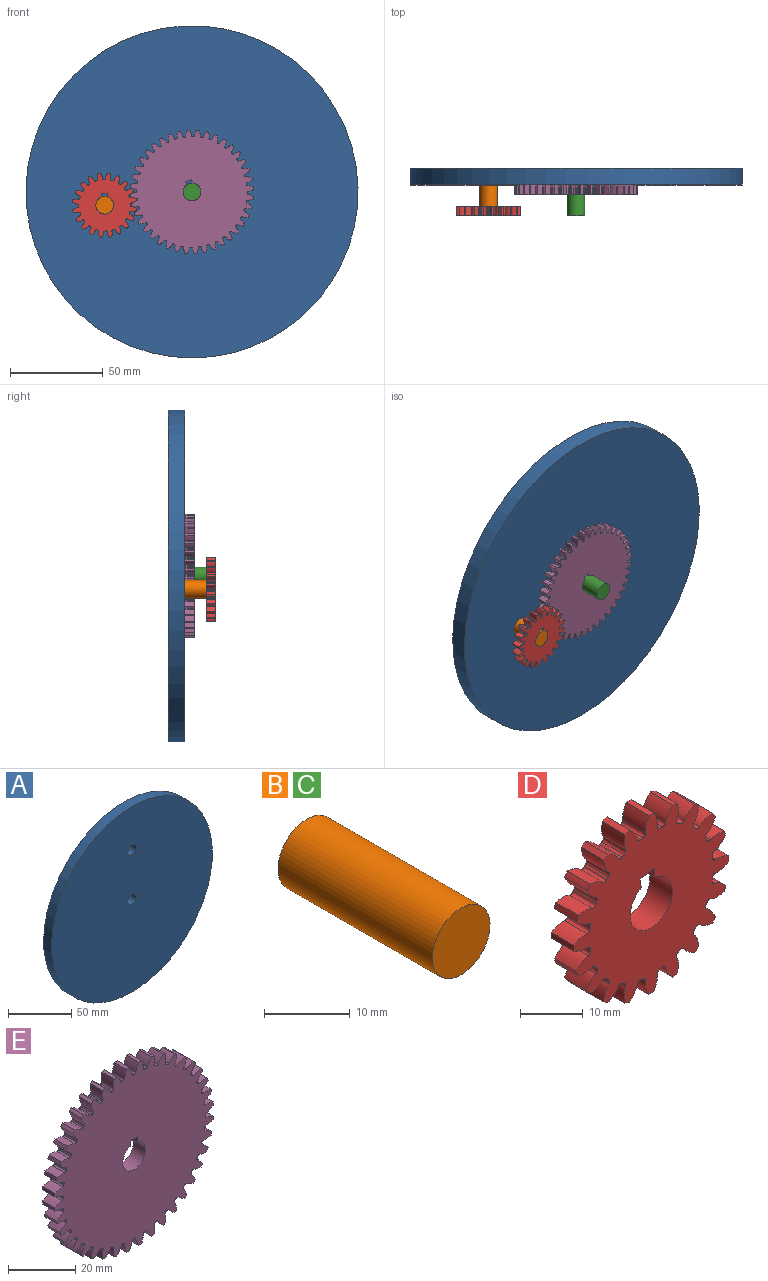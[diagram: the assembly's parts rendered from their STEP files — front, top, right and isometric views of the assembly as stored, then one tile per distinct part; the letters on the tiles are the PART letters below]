
ASSEMBLY  parts=5 mates=4
PART A: 5 faces, bbox 179.1x8.9x179.1 mm
  f0: cylinder r=4.76mm len=9.53mm, axis (0,1,0), area 266mm2, adj f3,f4
  f1: cylinder r=4.76mm len=9.53mm, axis (0,1,0), area 266mm2, adj f3,f4
  f2: cylinder r=89.55mm len=179.1mm, axis (0,1,0), area 5002mm2, adj f3,f4
  f3: plane 179.1x179.1mm, normal (0,-1,0), area 25049.8mm2, adj f0,f1,f2
  f4: plane 179.1x179.1mm, normal (0,1,0), area 25049.8mm2, adj f0,f1,f2
PART B: 3 faces, bbox 9.5x25.4x9.5 mm
  f0: cylinder r=4.76mm len=25.4mm, axis (0,1,0), area 760.1mm2, adj f1,f2
  f1: plane 9.53x9.53mm, normal (0,-1,0), area 71.3mm2, adj f0
  f2: plane 9.53x9.53mm, normal (0,1,0), area 71.3mm2, adj f0
PART C: same geometry as B
PART D: 126 faces, bbox 34.9x5.1x34.9 mm
  f0: cylinder r=17.46mm len=5.08mm, axis (0,1,0), area 5.6mm2, adj f19,f25,f76,f123
  f1: cylinder r=17.46mm len=5.08mm, axis (0,1,0), area 5.6mm2, adj f19,f25,f118,f121
  f2: cylinder r=17.46mm len=5.08mm, axis (0,1,0), area 5.6mm2, adj f19,f25,f113,f116
  f3: cylinder r=17.46mm len=5.08mm, axis (0,1,0), area 5.6mm2, adj f19,f25,f108,f111
  f4: cylinder r=17.46mm len=5.08mm, axis (0,1,0), area 5.6mm2, adj f19,f25,f103,f106
  f5: cylinder r=17.46mm len=5.08mm, axis (0,1,0), area 5.6mm2, adj f19,f25,f98,f101
  f6: cylinder r=17.46mm len=5.08mm, axis (0,1,0), area 5.6mm2, adj f19,f25,f93,f96
  f7: cylinder r=17.46mm len=5.08mm, axis (0,1,0), area 5.6mm2, adj f19,f25,f88,f91
  f8: cylinder r=17.46mm len=5.08mm, axis (0,1,0), area 5.6mm2, adj f19,f25,f71,f83
  f9: cylinder r=17.46mm len=5.08mm, axis (0,1,0), area 5.6mm2, adj f19,f25,f78,f81
  f10: cylinder r=17.46mm len=5.08mm, axis (0,1,0), area 5.6mm2, adj f19,f25,f66,f73
  f11: cylinder r=17.46mm len=5.08mm, axis (0,1,0), area 5.6mm2, adj f19,f25,f46,f68
  f12: cylinder r=17.46mm len=5.08mm, axis (0,1,0), area 5.6mm2, adj f19,f25,f26,f63
  f13: cylinder r=17.46mm len=5.08mm, axis (0,1,0), area 5.6mm2, adj f19,f25,f58,f61
  f14: cylinder r=17.46mm len=5.08mm, axis (0,1,0), area 5.6mm2, adj f19,f25,f53,f56
  f15: cylinder r=17.46mm len=5.08mm, axis (0,1,0), area 5.6mm2, adj f19,f25,f48,f51
  f16: cylinder r=17.46mm len=5.08mm, axis (0,1,0), area 5.6mm2, adj f19,f25,f36,f43
  f17: cylinder r=17.46mm len=5.08mm, axis (0,1,0), area 5.6mm2, adj f19,f25,f38,f86
  f18: cylinder r=17.46mm len=5.08mm, axis (0,1,0), area 5.6mm2, adj f19,f25,f33,f41
  f19: plane 34.94x34.94mm, normal (0,-1,0), area 699.1mm2, adj f0,f1,f2,f3,f4,f5,f6,f7
  f20: plane 5.08x1.84mm, normal (-0.99,0,-0.16), area 9.4mm2, adj f19,f21,f23,f25
  f21: cylinder r=4.76mm len=9.53mm, axis (0,1,0), area 135.6mm2, adj f19,f20,f22,f25
  f22: plane 5.08x1.84mm, normal (0.99,0,0.16), area 9.4mm2, adj f19,f21,f23,f25
  f23: plane 5.08x3.14mm, normal (0.16,0,-0.99), area 16.1mm2, adj f19,f20,f22,f25
  f24: cylinder r=17.46mm len=5.08mm, axis (0,1,0), area 5.6mm2, adj f19,f25,f28,f31
  f25: plane 34.94x34.94mm, normal (0,1,0), area 699.1mm2, adj f0,f1,f2,f3,f4,f5,f6,f7
  f26: extruded ~5.08x2.62mm, area 16.2mm2, adj f12,f19,f25,f29
  f27: cylinder r=13.89mm len=5.08mm, axis (0,1,0), area 2.9mm2, adj f19,f25,f29,f30
  f28: extruded ~5.08x3.01mm, area 16.2mm2, adj f19,f24,f25,f30
  f29: cylinder r=0.63mm len=5.08mm, axis (0,1,0), area 4.9mm2, adj f19,f25,f26,f27
  f30: cylinder r=0.63mm len=5.08mm, axis (0,1,0), area 4.9mm2, adj f19,f25,f27,f28
  f31: extruded ~5.08x3.01mm, area 16.2mm2, adj f19,f24,f25,f34
  f32: cylinder r=13.89mm len=5.08mm, axis (0,1,0), area 2.9mm2, adj f19,f25,f34,f35
  f33: extruded ~5.08x2.62mm, area 16.2mm2, adj f18,f19,f25,f35
  f34: cylinder r=0.63mm len=5.08mm, axis (0,1,0), area 4.9mm2, adj f19,f25,f31,f32
  f35: cylinder r=0.63mm len=5.08mm, axis (0,1,0), area 4.9mm2, adj f19,f25,f32,f33
  f36: extruded ~5.08x2.91mm, area 16.2mm2, adj f16,f19,f25,f39
  f37: cylinder r=13.89mm len=5.08mm, axis (0,1,0), area 2.9mm2, adj f19,f25,f39,f40
  f38: extruded ~5.08x2.91mm, area 16.2mm2, adj f17,f19,f25,f40
  f39: cylinder r=0.63mm len=5.08mm, axis (0,1,0), area 4.9mm2, adj f19,f25,f36,f37
  f40: cylinder r=0.63mm len=5.08mm, axis (0,1,0), area 4.9mm2, adj f19,f25,f37,f38
  f41: extruded ~5.08x3.11mm, area 16.2mm2, adj f18,f19,f25,f44
  f42: cylinder r=13.89mm len=5.08mm, axis (0,1,0), area 2.9mm2, adj f19,f25,f44,f45
  f43: extruded ~5.08x2.42mm, area 16.2mm2, adj f16,f19,f25,f45
  f44: cylinder r=0.63mm len=5.08mm, axis (0,1,0), area 4.9mm2, adj f19,f25,f41,f42
  f45: cylinder r=0.63mm len=5.08mm, axis (0,1,0), area 4.9mm2, adj f19,f25,f42,f43
  f46: extruded ~5.08x3.01mm, area 16.2mm2, adj f11,f19,f25,f49
  f47: cylinder r=13.89mm len=5.08mm, axis (0,1,0), area 2.9mm2, adj f19,f25,f49,f50
  f48: extruded ~5.08x2.62mm, area 16.2mm2, adj f15,f19,f25,f50
  f49: cylinder r=0.63mm len=5.08mm, axis (0,1,0), area 4.9mm2, adj f19,f25,f46,f47
  f50: cylinder r=0.63mm len=5.08mm, axis (0,1,0), area 4.9mm2, adj f19,f25,f47,f48
  f51: extruded ~5.08x3.11mm, area 16.2mm2, adj f15,f19,f25,f54
  f52: cylinder r=13.89mm len=5.08mm, axis (0,1,0), area 2.9mm2, adj f19,f25,f54,f55
  f53: extruded ~5.08x2.42mm, area 16.2mm2, adj f14,f19,f25,f55
  f54: cylinder r=0.63mm len=5.08mm, axis (0,1,0), area 4.9mm2, adj f19,f25,f51,f52
  f55: cylinder r=0.63mm len=5.08mm, axis (0,1,0), area 4.9mm2, adj f19,f25,f52,f53
  f56: extruded ~5.08x2.91mm, area 16.2mm2, adj f14,f19,f25,f59
  f57: cylinder r=13.89mm len=5.08mm, axis (0,1,0), area 2.9mm2, adj f19,f25,f59,f60
  f58: extruded ~5.08x2.91mm, area 16.2mm2, adj f13,f19,f25,f60
  f59: cylinder r=0.63mm len=5.08mm, axis (0,1,0), area 4.9mm2, adj f19,f25,f56,f57
  f60: cylinder r=0.63mm len=5.08mm, axis (0,1,0), area 4.9mm2, adj f19,f25,f57,f58
  f61: extruded ~5.08x2.42mm, area 16.2mm2, adj f13,f19,f25,f64
  f62: cylinder r=13.89mm len=5.08mm, axis (0,1,0), area 2.9mm2, adj f19,f25,f64,f65
  f63: extruded ~5.08x3.11mm, area 16.2mm2, adj f12,f19,f25,f65
  f64: cylinder r=0.63mm len=5.08mm, axis (0,1,0), area 4.9mm2, adj f19,f25,f61,f62
  f65: cylinder r=0.63mm len=5.08mm, axis (0,1,0), area 4.9mm2, adj f19,f25,f62,f63
  f66: extruded ~5.08x2.62mm, area 16.2mm2, adj f10,f19,f25,f69
  f67: cylinder r=13.89mm len=5.08mm, axis (0,1,0), area 2.9mm2, adj f19,f25,f69,f70
  f68: extruded ~5.08x3.01mm, area 16.2mm2, adj f11,f19,f25,f70
  f69: cylinder r=0.63mm len=5.08mm, axis (0,1,0), area 4.9mm2, adj f19,f25,f66,f67
  f70: cylinder r=0.63mm len=5.08mm, axis (0,1,0), area 4.9mm2, adj f19,f25,f67,f68
  f71: extruded ~5.08x2.42mm, area 16.2mm2, adj f8,f19,f25,f74
  f72: cylinder r=13.89mm len=5.08mm, axis (0,1,0), area 2.9mm2, adj f19,f25,f74,f75
  f73: extruded ~5.08x3.11mm, area 16.2mm2, adj f10,f19,f25,f75
  f74: cylinder r=0.63mm len=5.08mm, axis (0,1,0), area 4.9mm2, adj f19,f25,f71,f72
  f75: cylinder r=0.63mm len=5.08mm, axis (0,1,0), area 4.9mm2, adj f19,f25,f72,f73
  f76: extruded ~5.08x3.11mm, area 16.2mm2, adj f0,f19,f25,f79
  f77: cylinder r=13.89mm len=5.08mm, axis (0,1,0), area 2.9mm2, adj f19,f25,f79,f80
  f78: extruded ~5.08x2.42mm, area 16.2mm2, adj f9,f19,f25,f80
  f79: cylinder r=0.63mm len=5.08mm, axis (0,1,0), area 4.9mm2, adj f19,f25,f76,f77
  f80: cylinder r=0.63mm len=5.08mm, axis (0,1,0), area 4.9mm2, adj f19,f25,f77,f78
  f81: extruded ~5.08x2.91mm, area 16.2mm2, adj f9,f19,f25,f84
  f82: cylinder r=13.89mm len=5.08mm, axis (0,1,0), area 2.9mm2, adj f19,f25,f84,f85
  f83: extruded ~5.08x2.91mm, area 16.2mm2, adj f8,f19,f25,f85
  f84: cylinder r=0.63mm len=5.08mm, axis (0,1,0), area 4.9mm2, adj f19,f25,f81,f82
  f85: cylinder r=0.63mm len=5.08mm, axis (0,1,0), area 4.9mm2, adj f19,f25,f82,f83
  f86: extruded ~5.08x2.42mm, area 16.2mm2, adj f17,f19,f25,f89
  f87: cylinder r=13.89mm len=5.08mm, axis (0,1,0), area 2.9mm2, adj f19,f25,f89,f90
  f88: extruded ~5.08x3.11mm, area 16.2mm2, adj f7,f19,f25,f90
  f89: cylinder r=0.63mm len=5.08mm, axis (0,1,0), area 4.9mm2, adj f19,f25,f86,f87
  f90: cylinder r=0.63mm len=5.08mm, axis (0,1,0), area 4.9mm2, adj f19,f25,f87,f88
  f91: extruded ~5.08x2.62mm, area 16.2mm2, adj f7,f19,f25,f94
  f92: cylinder r=13.89mm len=5.08mm, axis (0,1,0), area 2.9mm2, adj f19,f25,f94,f95
  f93: extruded ~5.08x3.01mm, area 16.2mm2, adj f6,f19,f25,f95
  f94: cylinder r=0.63mm len=5.08mm, axis (0,1,0), area 4.9mm2, adj f19,f25,f91,f92
  f95: cylinder r=0.63mm len=5.08mm, axis (0,1,0), area 4.9mm2, adj f19,f25,f92,f93
  f96: extruded ~5.08x3.01mm, area 16.2mm2, adj f6,f19,f25,f99
  f97: cylinder r=13.89mm len=5.08mm, axis (0,1,0), area 2.9mm2, adj f19,f25,f99,f100
  f98: extruded ~5.08x2.62mm, area 16.2mm2, adj f5,f19,f25,f100
  f99: cylinder r=0.63mm len=5.08mm, axis (0,1,0), area 4.9mm2, adj f19,f25,f96,f97
  f100: cylinder r=0.63mm len=5.08mm, axis (0,1,0), area 4.9mm2, adj f19,f25,f97,f98
  f101: extruded ~5.08x3.11mm, area 16.2mm2, adj f5,f19,f25,f104
  f102: cylinder r=13.89mm len=5.08mm, axis (0,1,0), area 2.9mm2, adj f19,f25,f104,f105
  f103: extruded ~5.08x2.42mm, area 16.2mm2, adj f4,f19,f25,f105
  f104: cylinder r=0.63mm len=5.08mm, axis (0,1,0), area 4.9mm2, adj f19,f25,f101,f102
  f105: cylinder r=0.63mm len=5.08mm, axis (0,1,0), area 4.9mm2, adj f19,f25,f102,f103
  f106: extruded ~5.08x2.91mm, area 16.2mm2, adj f4,f19,f25,f109
  f107: cylinder r=13.89mm len=5.08mm, axis (0,1,0), area 2.9mm2, adj f19,f25,f109,f110
  f108: extruded ~5.08x2.91mm, area 16.2mm2, adj f3,f19,f25,f110
  f109: cylinder r=0.63mm len=5.08mm, axis (0,1,0), area 4.9mm2, adj f19,f25,f106,f107
  f110: cylinder r=0.63mm len=5.08mm, axis (0,1,0), area 4.9mm2, adj f19,f25,f107,f108
  f111: extruded ~5.08x2.42mm, area 16.2mm2, adj f3,f19,f25,f114
  f112: cylinder r=13.89mm len=5.08mm, axis (0,1,0), area 2.9mm2, adj f19,f25,f114,f115
  f113: extruded ~5.08x3.11mm, area 16.2mm2, adj f2,f19,f25,f115
  f114: cylinder r=0.63mm len=5.08mm, axis (0,1,0), area 4.9mm2, adj f19,f25,f111,f112
  f115: cylinder r=0.63mm len=5.08mm, axis (0,1,0), area 4.9mm2, adj f19,f25,f112,f113
  f116: extruded ~5.08x2.62mm, area 16.2mm2, adj f2,f19,f25,f119
  f117: cylinder r=13.89mm len=5.08mm, axis (0,1,0), area 2.9mm2, adj f19,f25,f119,f120
  f118: extruded ~5.08x3.01mm, area 16.2mm2, adj f1,f19,f25,f120
  f119: cylinder r=0.63mm len=5.08mm, axis (0,1,0), area 4.9mm2, adj f19,f25,f116,f117
  f120: cylinder r=0.63mm len=5.08mm, axis (0,1,0), area 4.9mm2, adj f19,f25,f117,f118
  f121: extruded ~5.08x3.01mm, area 16.2mm2, adj f1,f19,f25,f124
  f122: cylinder r=13.89mm len=5.08mm, axis (0,1,0), area 2.9mm2, adj f19,f25,f124,f125
  f123: extruded ~5.08x2.62mm, area 16.2mm2, adj f0,f19,f25,f125
  f124: cylinder r=0.63mm len=5.08mm, axis (0,1,0), area 4.9mm2, adj f19,f25,f121,f122
  f125: cylinder r=0.63mm len=5.08mm, axis (0,1,0), area 4.9mm2, adj f19,f25,f122,f123
PART E: 246 faces, bbox 66.6x5.1x66.6 mm
  f0: cylinder r=33.34mm len=5.08mm, axis (0,1,0), area 6.1mm2, adj f39,f45,f151,f243
  f1: cylinder r=33.34mm len=5.08mm, axis (0,1,0), area 6.1mm2, adj f39,f45,f238,f241
  f2: cylinder r=33.34mm len=5.08mm, axis (0,1,0), area 6.1mm2, adj f39,f45,f233,f236
  f3: cylinder r=33.34mm len=5.08mm, axis (0,1,0), area 6.1mm2, adj f39,f45,f228,f231
  f4: cylinder r=33.34mm len=5.08mm, axis (0,1,0), area 6.1mm2, adj f39,f45,f223,f226
  f5: cylinder r=33.34mm len=5.08mm, axis (0,1,0), area 6.1mm2, adj f39,f45,f218,f221
  f6: cylinder r=33.34mm len=5.08mm, axis (0,1,0), area 6.1mm2, adj f39,f45,f213,f216
  f7: cylinder r=33.34mm len=5.08mm, axis (0,1,0), area 6.1mm2, adj f39,f45,f208,f211
  f8: cylinder r=33.34mm len=5.08mm, axis (0,1,0), area 6.1mm2, adj f39,f45,f196,f203
  f9: cylinder r=33.34mm len=5.08mm, axis (0,1,0), area 6.1mm2, adj f39,f45,f198,f206
  f10: cylinder r=33.34mm len=5.08mm, axis (0,1,0), area 6.1mm2, adj f39,f45,f193,f201
  f11: cylinder r=33.34mm len=5.08mm, axis (0,1,0), area 6.1mm2, adj f39,f45,f188,f191
  f12: cylinder r=33.34mm len=5.08mm, axis (0,1,0), area 6.1mm2, adj f39,f45,f183,f186
  f13: cylinder r=33.34mm len=5.08mm, axis (0,1,0), area 6.1mm2, adj f39,f45,f178,f181
  f14: cylinder r=33.34mm len=5.08mm, axis (0,1,0), area 6.1mm2, adj f39,f45,f173,f176
  f15: cylinder r=33.34mm len=5.08mm, axis (0,1,0), area 6.1mm2, adj f39,f45,f168,f171
  f16: cylinder r=33.34mm len=5.08mm, axis (0,1,0), area 6.1mm2, adj f39,f45,f141,f163
  f17: cylinder r=33.34mm len=5.08mm, axis (0,1,0), area 6.1mm2, adj f39,f45,f158,f161
  f18: cylinder r=33.34mm len=5.08mm, axis (0,1,0), area 6.1mm2, adj f39,f45,f146,f153
  f19: cylinder r=33.34mm len=5.08mm, axis (0,1,0), area 6.1mm2, adj f39,f45,f148,f156
  f20: cylinder r=33.34mm len=5.08mm, axis (0,1,0), area 6.1mm2, adj f39,f45,f136,f143
  f21: cylinder r=33.34mm len=5.08mm, axis (0,1,0), area 6.1mm2, adj f39,f45,f131,f138
  f22: cylinder r=33.34mm len=5.08mm, axis (0,1,0), area 6.1mm2, adj f39,f45,f126,f133
  f23: cylinder r=33.34mm len=5.08mm, axis (0,1,0), area 6.1mm2, adj f39,f45,f86,f128
  f24: cylinder r=33.34mm len=5.08mm, axis (0,1,0), area 6.1mm2, adj f39,f45,f46,f123
  f25: cylinder r=33.34mm len=5.08mm, axis (0,1,0), area 6.1mm2, adj f39,f45,f118,f121
  f26: cylinder r=33.34mm len=5.08mm, axis (0,1,0), area 6.1mm2, adj f39,f45,f113,f116
  f27: cylinder r=33.34mm len=5.08mm, axis (0,1,0), area 6.1mm2, adj f39,f45,f108,f111
  f28: cylinder r=33.34mm len=5.08mm, axis (0,1,0), area 6.1mm2, adj f39,f45,f96,f103
  f29: cylinder r=33.34mm len=5.08mm, axis (0,1,0), area 6.1mm2, adj f39,f45,f98,f106
  f30: cylinder r=33.34mm len=5.08mm, axis (0,1,0), area 6.1mm2, adj f39,f45,f93,f101
  f31: cylinder r=33.34mm len=5.08mm, axis (0,1,0), area 6.1mm2, adj f39,f45,f88,f91
  f32: cylinder r=33.34mm len=5.08mm, axis (0,1,0), area 6.1mm2, adj f39,f45,f71,f83
  f33: cylinder r=33.34mm len=5.08mm, axis (0,1,0), area 6.1mm2, adj f39,f45,f78,f81
  f34: cylinder r=33.34mm len=5.08mm, axis (0,1,0), area 6.1mm2, adj f39,f45,f66,f73
  f35: cylinder r=33.34mm len=5.08mm, axis (0,1,0), area 6.1mm2, adj f39,f45,f68,f166
  f36: cylinder r=33.34mm len=5.08mm, axis (0,1,0), area 6.1mm2, adj f39,f45,f63,f76
  f37: cylinder r=33.34mm len=5.08mm, axis (0,1,0), area 6.1mm2, adj f39,f45,f58,f61
  f38: cylinder r=33.34mm len=5.08mm, axis (0,1,0), area 6.1mm2, adj f39,f45,f53,f56
  f39: plane 66.55x66.55mm, normal (0,-1,0), area 3066.7mm2, adj f0,f1,f2,f3,f4,f5,f6,f7
  f40: plane 5.08x1.86mm, normal (-1,0,0), area 9.4mm2, adj f39,f41,f43,f45
  f41: cylinder r=4.76mm len=9.53mm, axis (0,1,0), area 135.6mm2, adj f39,f40,f42,f45
  f42: plane 5.08x1.86mm, normal (1,0,0), area 9.4mm2, adj f39,f41,f43,f45
  f43: plane 5.08x3.18mm, normal (0,0,-1), area 16.1mm2, adj f39,f40,f42,f45
  f44: cylinder r=33.34mm len=5.08mm, axis (0,1,0), area 6.1mm2, adj f39,f45,f48,f51
  f45: plane 66.55x66.55mm, normal (0,1,0), area 3066.7mm2, adj f0,f1,f2,f3,f4,f5,f6,f7
  f46: extruded ~5.08x3.06mm, area 16.8mm2, adj f24,f39,f45,f49
  f47: cylinder r=29.77mm len=5.08mm, axis (0,1,0), area 2.3mm2, adj f39,f45,f49,f50
  f48: extruded ~5.08x3.06mm, area 16.8mm2, adj f39,f44,f45,f50
  f49: cylinder r=0.56mm len=5.08mm, axis (0,1,0), area 4mm2, adj f39,f45,f46,f47
  f50: cylinder r=0.56mm len=5.08mm, axis (0,1,0), area 4mm2, adj f39,f45,f47,f48
  f51: extruded ~5.08x3.21mm, area 16.8mm2, adj f39,f44,f45,f54
  f52: cylinder r=29.77mm len=5.08mm, axis (0,1,0), area 2.3mm2, adj f39,f45,f54,f55
  f53: extruded ~5.08x2.82mm, area 16.8mm2, adj f38,f39,f45,f55
  f54: cylinder r=0.56mm len=5.08mm, axis (0,1,0), area 4mm2, adj f39,f45,f51,f52
  f55: cylinder r=0.56mm len=5.08mm, axis (0,1,0), area 4mm2, adj f39,f45,f52,f53
  f56: extruded ~5.08x3.29mm, area 16.8mm2, adj f38,f39,f45,f59
  f57: cylinder r=29.77mm len=5.08mm, axis (0,1,0), area 2.3mm2, adj f39,f45,f59,f60
  f58: extruded ~5.08x2.52mm, area 16.8mm2, adj f37,f39,f45,f60
  f59: cylinder r=0.56mm len=5.08mm, axis (0,1,0), area 4mm2, adj f39,f45,f56,f57
  f60: cylinder r=0.56mm len=5.08mm, axis (0,1,0), area 4mm2, adj f39,f45,f57,f58
  f61: extruded ~5.08x3.28mm, area 16.8mm2, adj f37,f39,f45,f64
  f62: cylinder r=29.77mm len=5.08mm, axis (0,1,0), area 2.3mm2, adj f39,f45,f64,f65
  f63: extruded ~5.08x2.49mm, area 16.8mm2, adj f36,f39,f45,f65
  f64: cylinder r=0.56mm len=5.08mm, axis (0,1,0), area 4mm2, adj f39,f45,f61,f62
  f65: cylinder r=0.56mm len=5.08mm, axis (0,1,0), area 4mm2, adj f39,f45,f62,f63
  f66: extruded ~5.08x2.49mm, area 16.8mm2, adj f34,f39,f45,f69
  f67: cylinder r=29.77mm len=5.08mm, axis (0,1,0), area 2.3mm2, adj f39,f45,f69,f70
  f68: extruded ~5.08x3.28mm, area 16.8mm2, adj f35,f39,f45,f70
  f69: cylinder r=0.56mm len=5.08mm, axis (0,1,0), area 4mm2, adj f39,f45,f66,f67
  f70: cylinder r=0.56mm len=5.08mm, axis (0,1,0), area 4mm2, adj f39,f45,f67,f68
  f71: extruded ~5.08x2.79mm, area 16.8mm2, adj f32,f39,f45,f74
  f72: cylinder r=29.77mm len=5.08mm, axis (0,1,0), area 2.3mm2, adj f39,f45,f74,f75
  f73: extruded ~5.08x3.2mm, area 16.8mm2, adj f34,f39,f45,f75
  f74: cylinder r=0.56mm len=5.08mm, axis (0,1,0), area 4mm2, adj f39,f45,f71,f72
  f75: cylinder r=0.56mm len=5.08mm, axis (0,1,0), area 4mm2, adj f39,f45,f72,f73
  f76: extruded ~5.08x3.2mm, area 16.8mm2, adj f36,f39,f45,f79
  f77: cylinder r=29.77mm len=5.08mm, axis (0,1,0), area 2.3mm2, adj f39,f45,f79,f80
  f78: extruded ~5.08x2.79mm, area 16.8mm2, adj f33,f39,f45,f80
  f79: cylinder r=0.56mm len=5.08mm, axis (0,1,0), area 4mm2, adj f39,f45,f76,f77
  f80: cylinder r=0.56mm len=5.08mm, axis (0,1,0), area 4mm2, adj f39,f45,f77,f78
  f81: extruded ~5.08x3.03mm, area 16.8mm2, adj f33,f39,f45,f84
  f82: cylinder r=29.77mm len=5.08mm, axis (0,1,0), area 2.3mm2, adj f39,f45,f84,f85
  f83: extruded ~5.08x3.03mm, area 16.8mm2, adj f32,f39,f45,f85
  f84: cylinder r=0.56mm len=5.08mm, axis (0,1,0), area 4mm2, adj f39,f45,f81,f82
  f85: cylinder r=0.56mm len=5.08mm, axis (0,1,0), area 4mm2, adj f39,f45,f82,f83
  f86: extruded ~5.08x3.29mm, area 16.8mm2, adj f23,f39,f45,f89
  f87: cylinder r=29.77mm len=5.08mm, axis (0,1,0), area 2.3mm2, adj f39,f45,f89,f90
  f88: extruded ~5.08x2.52mm, area 16.8mm2, adj f31,f39,f45,f90
  f89: cylinder r=0.56mm len=5.08mm, axis (0,1,0), area 4mm2, adj f39,f45,f86,f87
  f90: cylinder r=0.56mm len=5.08mm, axis (0,1,0), area 4mm2, adj f39,f45,f87,f88
  f91: extruded ~5.08x3.28mm, area 16.8mm2, adj f31,f39,f45,f94
  f92: cylinder r=29.77mm len=5.08mm, axis (0,1,0), area 2.3mm2, adj f39,f45,f94,f95
  f93: extruded ~5.08x2.49mm, area 16.8mm2, adj f30,f39,f45,f95
  f94: cylinder r=0.56mm len=5.08mm, axis (0,1,0), area 4mm2, adj f39,f45,f91,f92
  f95: cylinder r=0.56mm len=5.08mm, axis (0,1,0), area 4mm2, adj f39,f45,f92,f93
  f96: extruded ~5.08x3.03mm, area 16.8mm2, adj f28,f39,f45,f99
  f97: cylinder r=29.77mm len=5.08mm, axis (0,1,0), area 2.3mm2, adj f39,f45,f99,f100
  f98: extruded ~5.08x3.03mm, area 16.8mm2, adj f29,f39,f45,f100
  f99: cylinder r=0.56mm len=5.08mm, axis (0,1,0), area 4mm2, adj f39,f45,f96,f97
  f100: cylinder r=0.56mm len=5.08mm, axis (0,1,0), area 4mm2, adj f39,f45,f97,f98
  f101: extruded ~5.08x3.2mm, area 16.8mm2, adj f30,f39,f45,f104
  f102: cylinder r=29.77mm len=5.08mm, axis (0,1,0), area 2.3mm2, adj f39,f45,f104,f105
  f103: extruded ~5.08x2.79mm, area 16.8mm2, adj f28,f39,f45,f105
  f104: cylinder r=0.56mm len=5.08mm, axis (0,1,0), area 4mm2, adj f39,f45,f101,f102
  f105: cylinder r=0.56mm len=5.08mm, axis (0,1,0), area 4mm2, adj f39,f45,f102,f103
  f106: extruded ~5.08x2.79mm, area 16.8mm2, adj f29,f39,f45,f109
  f107: cylinder r=29.77mm len=5.08mm, axis (0,1,0), area 2.3mm2, adj f39,f45,f109,f110
  f108: extruded ~5.08x3.2mm, area 16.8mm2, adj f27,f39,f45,f110
  f109: cylinder r=0.56mm len=5.08mm, axis (0,1,0), area 4mm2, adj f39,f45,f106,f107
  f110: cylinder r=0.56mm len=5.08mm, axis (0,1,0), area 4mm2, adj f39,f45,f107,f108
  f111: extruded ~5.08x2.49mm, area 16.8mm2, adj f27,f39,f45,f114
  f112: cylinder r=29.77mm len=5.08mm, axis (0,1,0), area 2.3mm2, adj f39,f45,f114,f115
  f113: extruded ~5.08x3.28mm, area 16.8mm2, adj f26,f39,f45,f115
  f114: cylinder r=0.56mm len=5.08mm, axis (0,1,0), area 4mm2, adj f39,f45,f111,f112
  f115: cylinder r=0.56mm len=5.08mm, axis (0,1,0), area 4mm2, adj f39,f45,f112,f113
  f116: extruded ~5.08x2.52mm, area 16.8mm2, adj f26,f39,f45,f119
  f117: cylinder r=29.77mm len=5.08mm, axis (0,1,0), area 2.3mm2, adj f39,f45,f119,f120
  f118: extruded ~5.08x3.29mm, area 16.8mm2, adj f25,f39,f45,f120
  f119: cylinder r=0.56mm len=5.08mm, axis (0,1,0), area 4mm2, adj f39,f45,f116,f117
  f120: cylinder r=0.56mm len=5.08mm, axis (0,1,0), area 4mm2, adj f39,f45,f117,f118
  f121: extruded ~5.08x2.82mm, area 16.8mm2, adj f25,f39,f45,f124
  f122: cylinder r=29.77mm len=5.08mm, axis (0,1,0), area 2.3mm2, adj f39,f45,f124,f125
  f123: extruded ~5.08x3.21mm, area 16.8mm2, adj f24,f39,f45,f125
  f124: cylinder r=0.56mm len=5.08mm, axis (0,1,0), area 4mm2, adj f39,f45,f121,f122
  f125: cylinder r=0.56mm len=5.08mm, axis (0,1,0), area 4mm2, adj f39,f45,f122,f123
  f126: extruded ~5.08x3.21mm, area 16.8mm2, adj f22,f39,f45,f129
  f127: cylinder r=29.77mm len=5.08mm, axis (0,1,0), area 2.3mm2, adj f39,f45,f129,f130
  f128: extruded ~5.08x2.82mm, area 16.8mm2, adj f23,f39,f45,f130
  f129: cylinder r=0.56mm len=5.08mm, axis (0,1,0), area 4mm2, adj f39,f45,f126,f127
  f130: cylinder r=0.56mm len=5.08mm, axis (0,1,0), area 4mm2, adj f39,f45,f127,f128
  f131: extruded ~5.08x3.06mm, area 16.8mm2, adj f21,f39,f45,f134
  f132: cylinder r=29.77mm len=5.08mm, axis (0,1,0), area 2.3mm2, adj f39,f45,f134,f135
  f133: extruded ~5.08x3.06mm, area 16.8mm2, adj f22,f39,f45,f135
  f134: cylinder r=0.56mm len=5.08mm, axis (0,1,0), area 4mm2, adj f39,f45,f131,f132
  f135: cylinder r=0.56mm len=5.08mm, axis (0,1,0), area 4mm2, adj f39,f45,f132,f133
  f136: extruded ~5.08x2.82mm, area 16.8mm2, adj f20,f39,f45,f139
  f137: cylinder r=29.77mm len=5.08mm, axis (0,1,0), area 2.3mm2, adj f39,f45,f139,f140
  f138: extruded ~5.08x3.21mm, area 16.8mm2, adj f21,f39,f45,f140
  f139: cylinder r=0.56mm len=5.08mm, axis (0,1,0), area 4mm2, adj f39,f45,f136,f137
  f140: cylinder r=0.56mm len=5.08mm, axis (0,1,0), area 4mm2, adj f39,f45,f137,f138
  f141: extruded ~5.08x2.52mm, area 16.8mm2, adj f16,f39,f45,f144
  f142: cylinder r=29.77mm len=5.08mm, axis (0,1,0), area 2.3mm2, adj f39,f45,f144,f145
  f143: extruded ~5.08x3.29mm, area 16.8mm2, adj f20,f39,f45,f145
  f144: cylinder r=0.56mm len=5.08mm, axis (0,1,0), area 4mm2, adj f39,f45,f141,f142
  f145: cylinder r=0.56mm len=5.08mm, axis (0,1,0), area 4mm2, adj f39,f45,f142,f143
  f146: extruded ~5.08x3.03mm, area 16.8mm2, adj f18,f39,f45,f149
  f147: cylinder r=29.77mm len=5.08mm, axis (0,1,0), area 2.3mm2, adj f39,f45,f149,f150
  f148: extruded ~5.08x3.03mm, area 16.8mm2, adj f19,f39,f45,f150
  f149: cylinder r=0.56mm len=5.08mm, axis (0,1,0), area 4mm2, adj f39,f45,f146,f147
  f150: cylinder r=0.56mm len=5.08mm, axis (0,1,0), area 4mm2, adj f39,f45,f147,f148
  f151: extruded ~5.08x3.2mm, area 16.8mm2, adj f0,f39,f45,f154
  f152: cylinder r=29.77mm len=5.08mm, axis (0,1,0), area 2.3mm2, adj f39,f45,f154,f155
  f153: extruded ~5.08x2.79mm, area 16.8mm2, adj f18,f39,f45,f155
  f154: cylinder r=0.56mm len=5.08mm, axis (0,1,0), area 4mm2, adj f39,f45,f151,f152
  f155: cylinder r=0.56mm len=5.08mm, axis (0,1,0), area 4mm2, adj f39,f45,f152,f153
  f156: extruded ~5.08x2.79mm, area 16.8mm2, adj f19,f39,f45,f159
  f157: cylinder r=29.77mm len=5.08mm, axis (0,1,0), area 2.3mm2, adj f39,f45,f159,f160
  f158: extruded ~5.08x3.2mm, area 16.8mm2, adj f17,f39,f45,f160
  f159: cylinder r=0.56mm len=5.08mm, axis (0,1,0), area 4mm2, adj f39,f45,f156,f157
  f160: cylinder r=0.56mm len=5.08mm, axis (0,1,0), area 4mm2, adj f39,f45,f157,f158
  f161: extruded ~5.08x2.49mm, area 16.8mm2, adj f17,f39,f45,f164
  f162: cylinder r=29.77mm len=5.08mm, axis (0,1,0), area 2.3mm2, adj f39,f45,f164,f165
  f163: extruded ~5.08x3.28mm, area 16.8mm2, adj f16,f39,f45,f165
  f164: cylinder r=0.56mm len=5.08mm, axis (0,1,0), area 4mm2, adj f39,f45,f161,f162
  f165: cylinder r=0.56mm len=5.08mm, axis (0,1,0), area 4mm2, adj f39,f45,f162,f163
  f166: extruded ~5.08x2.52mm, area 16.8mm2, adj f35,f39,f45,f169
  f167: cylinder r=29.77mm len=5.08mm, axis (0,1,0), area 2.3mm2, adj f39,f45,f169,f170
  f168: extruded ~5.08x3.29mm, area 16.8mm2, adj f15,f39,f45,f170
  f169: cylinder r=0.56mm len=5.08mm, axis (0,1,0), area 4mm2, adj f39,f45,f166,f167
  f170: cylinder r=0.56mm len=5.08mm, axis (0,1,0), area 4mm2, adj f39,f45,f167,f168
  f171: extruded ~5.08x2.82mm, area 16.8mm2, adj f15,f39,f45,f174
  f172: cylinder r=29.77mm len=5.08mm, axis (0,1,0), area 2.3mm2, adj f39,f45,f174,f175
  f173: extruded ~5.08x3.21mm, area 16.8mm2, adj f14,f39,f45,f175
  f174: cylinder r=0.56mm len=5.08mm, axis (0,1,0), area 4mm2, adj f39,f45,f171,f172
  f175: cylinder r=0.56mm len=5.08mm, axis (0,1,0), area 4mm2, adj f39,f45,f172,f173
  f176: extruded ~5.08x3.06mm, area 16.8mm2, adj f14,f39,f45,f179
  f177: cylinder r=29.77mm len=5.08mm, axis (0,1,0), area 2.3mm2, adj f39,f45,f179,f180
  f178: extruded ~5.08x3.06mm, area 16.8mm2, adj f13,f39,f45,f180
  f179: cylinder r=0.56mm len=5.08mm, axis (0,1,0), area 4mm2, adj f39,f45,f176,f177
  f180: cylinder r=0.56mm len=5.08mm, axis (0,1,0), area 4mm2, adj f39,f45,f177,f178
  f181: extruded ~5.08x3.21mm, area 16.8mm2, adj f13,f39,f45,f184
  f182: cylinder r=29.77mm len=5.08mm, axis (0,1,0), area 2.3mm2, adj f39,f45,f184,f185
  f183: extruded ~5.08x2.82mm, area 16.8mm2, adj f12,f39,f45,f185
  f184: cylinder r=0.56mm len=5.08mm, axis (0,1,0), area 4mm2, adj f39,f45,f181,f182
  f185: cylinder r=0.56mm len=5.08mm, axis (0,1,0), area 4mm2, adj f39,f45,f182,f183
  f186: extruded ~5.08x3.29mm, area 16.8mm2, adj f12,f39,f45,f189
  f187: cylinder r=29.77mm len=5.08mm, axis (0,1,0), area 2.3mm2, adj f39,f45,f189,f190
  f188: extruded ~5.08x2.52mm, area 16.8mm2, adj f11,f39,f45,f190
  f189: cylinder r=0.56mm len=5.08mm, axis (0,1,0), area 4mm2, adj f39,f45,f186,f187
  f190: cylinder r=0.56mm len=5.08mm, axis (0,1,0), area 4mm2, adj f39,f45,f187,f188
  f191: extruded ~5.08x3.28mm, area 16.8mm2, adj f11,f39,f45,f194
  f192: cylinder r=29.77mm len=5.08mm, axis (0,1,0), area 2.3mm2, adj f39,f45,f194,f195
  f193: extruded ~5.08x2.49mm, area 16.8mm2, adj f10,f39,f45,f195
  f194: cylinder r=0.56mm len=5.08mm, axis (0,1,0), area 4mm2, adj f39,f45,f191,f192
  f195: cylinder r=0.56mm len=5.08mm, axis (0,1,0), area 4mm2, adj f39,f45,f192,f193
  f196: extruded ~5.08x3.03mm, area 16.8mm2, adj f8,f39,f45,f199
  f197: cylinder r=29.77mm len=5.08mm, axis (0,1,0), area 2.3mm2, adj f39,f45,f199,f200
  f198: extruded ~5.08x3.03mm, area 16.8mm2, adj f9,f39,f45,f200
  f199: cylinder r=0.56mm len=5.08mm, axis (0,1,0), area 4mm2, adj f39,f45,f196,f197
  f200: cylinder r=0.56mm len=5.08mm, axis (0,1,0), area 4mm2, adj f39,f45,f197,f198
  f201: extruded ~5.08x3.2mm, area 16.8mm2, adj f10,f39,f45,f204
  f202: cylinder r=29.77mm len=5.08mm, axis (0,1,0), area 2.3mm2, adj f39,f45,f204,f205
  f203: extruded ~5.08x2.79mm, area 16.8mm2, adj f8,f39,f45,f205
  f204: cylinder r=0.56mm len=5.08mm, axis (0,1,0), area 4mm2, adj f39,f45,f201,f202
  f205: cylinder r=0.56mm len=5.08mm, axis (0,1,0), area 4mm2, adj f39,f45,f202,f203
  f206: extruded ~5.08x2.79mm, area 16.8mm2, adj f9,f39,f45,f209
  f207: cylinder r=29.77mm len=5.08mm, axis (0,1,0), area 2.3mm2, adj f39,f45,f209,f210
  f208: extruded ~5.08x3.2mm, area 16.8mm2, adj f7,f39,f45,f210
  f209: cylinder r=0.56mm len=5.08mm, axis (0,1,0), area 4mm2, adj f39,f45,f206,f207
  f210: cylinder r=0.56mm len=5.08mm, axis (0,1,0), area 4mm2, adj f39,f45,f207,f208
  f211: extruded ~5.08x2.49mm, area 16.8mm2, adj f7,f39,f45,f214
  f212: cylinder r=29.77mm len=5.08mm, axis (0,1,0), area 2.3mm2, adj f39,f45,f214,f215
  f213: extruded ~5.08x3.28mm, area 16.8mm2, adj f6,f39,f45,f215
  f214: cylinder r=0.56mm len=5.08mm, axis (0,1,0), area 4mm2, adj f39,f45,f211,f212
  f215: cylinder r=0.56mm len=5.08mm, axis (0,1,0), area 4mm2, adj f39,f45,f212,f213
  f216: extruded ~5.08x2.52mm, area 16.8mm2, adj f6,f39,f45,f219
  f217: cylinder r=29.77mm len=5.08mm, axis (0,1,0), area 2.3mm2, adj f39,f45,f219,f220
  f218: extruded ~5.08x3.29mm, area 16.8mm2, adj f5,f39,f45,f220
  f219: cylinder r=0.56mm len=5.08mm, axis (0,1,0), area 4mm2, adj f39,f45,f216,f217
  f220: cylinder r=0.56mm len=5.08mm, axis (0,1,0), area 4mm2, adj f39,f45,f217,f218
  f221: extruded ~5.08x2.82mm, area 16.8mm2, adj f5,f39,f45,f224
  f222: cylinder r=29.77mm len=5.08mm, axis (0,1,0), area 2.3mm2, adj f39,f45,f224,f225
  f223: extruded ~5.08x3.21mm, area 16.8mm2, adj f4,f39,f45,f225
  f224: cylinder r=0.56mm len=5.08mm, axis (0,1,0), area 4mm2, adj f39,f45,f221,f222
  f225: cylinder r=0.56mm len=5.08mm, axis (0,1,0), area 4mm2, adj f39,f45,f222,f223
  f226: extruded ~5.08x3.06mm, area 16.8mm2, adj f4,f39,f45,f229
  f227: cylinder r=29.77mm len=5.08mm, axis (0,1,0), area 2.3mm2, adj f39,f45,f229,f230
  f228: extruded ~5.08x3.06mm, area 16.8mm2, adj f3,f39,f45,f230
  f229: cylinder r=0.56mm len=5.08mm, axis (0,1,0), area 4mm2, adj f39,f45,f226,f227
  f230: cylinder r=0.56mm len=5.08mm, axis (0,1,0), area 4mm2, adj f39,f45,f227,f228
  f231: extruded ~5.08x3.21mm, area 16.8mm2, adj f3,f39,f45,f234
  f232: cylinder r=29.77mm len=5.08mm, axis (0,1,0), area 2.3mm2, adj f39,f45,f234,f235
  f233: extruded ~5.08x2.82mm, area 16.8mm2, adj f2,f39,f45,f235
  f234: cylinder r=0.56mm len=5.08mm, axis (0,1,0), area 4mm2, adj f39,f45,f231,f232
  f235: cylinder r=0.56mm len=5.08mm, axis (0,1,0), area 4mm2, adj f39,f45,f232,f233
  f236: extruded ~5.08x3.29mm, area 16.8mm2, adj f2,f39,f45,f239
  f237: cylinder r=29.77mm len=5.08mm, axis (0,1,0), area 2.3mm2, adj f39,f45,f239,f240
  f238: extruded ~5.08x2.52mm, area 16.8mm2, adj f1,f39,f45,f240
  f239: cylinder r=0.56mm len=5.08mm, axis (0,1,0), area 4mm2, adj f39,f45,f236,f237
  f240: cylinder r=0.56mm len=5.08mm, axis (0,1,0), area 4mm2, adj f39,f45,f237,f238
  f241: extruded ~5.08x3.28mm, area 16.8mm2, adj f1,f39,f45,f244
  f242: cylinder r=29.77mm len=5.08mm, axis (0,1,0), area 2.3mm2, adj f39,f45,f244,f245
  f243: extruded ~5.08x2.49mm, area 16.8mm2, adj f0,f39,f45,f245
  f244: cylinder r=0.56mm len=5.08mm, axis (0,1,0), area 4mm2, adj f39,f45,f241,f242
  f245: cylinder r=0.56mm len=5.08mm, axis (0,1,0), area 4mm2, adj f39,f45,f242,f243
PLACE A rot(axis=(0,-1,0),98.7deg) t=(-115.7,-21.69,-176.88)mm
PLACE B rot(axis=(0,-1,0),8.7deg) t=(-45.35,-21.69,-15.82)mm
PLACE C rot(axis=(0,-1,0),3.6deg) t=(3.28,-21.69,-14.99)mm fixed
PLACE D rot(axis=(0,1,0),7.6deg) t=(-114.68,-42.01,-31.38)mm
PLACE E rot(axis=(0,-1,0),16.9deg) t=(-88.25,-30.58,36.98)mm fixed
MATE revolute C.f0 <-> A.f0  axis (0,1,0) through (-68.98,-21.69,-29.1)mm
MATE revolute E.f0 <-> A.f0  axis (0,1,0) through (-68.98,-30.58,-29.1)mm
MATE revolute B.f0 <-> D.f0  axis (0,-1,0) through (-116.05,-47.09,-36.32)mm
MATE fastened B.f0 <-> A.f1  axis (0,1,0) through (-116.05,-21.69,-36.32)mm
